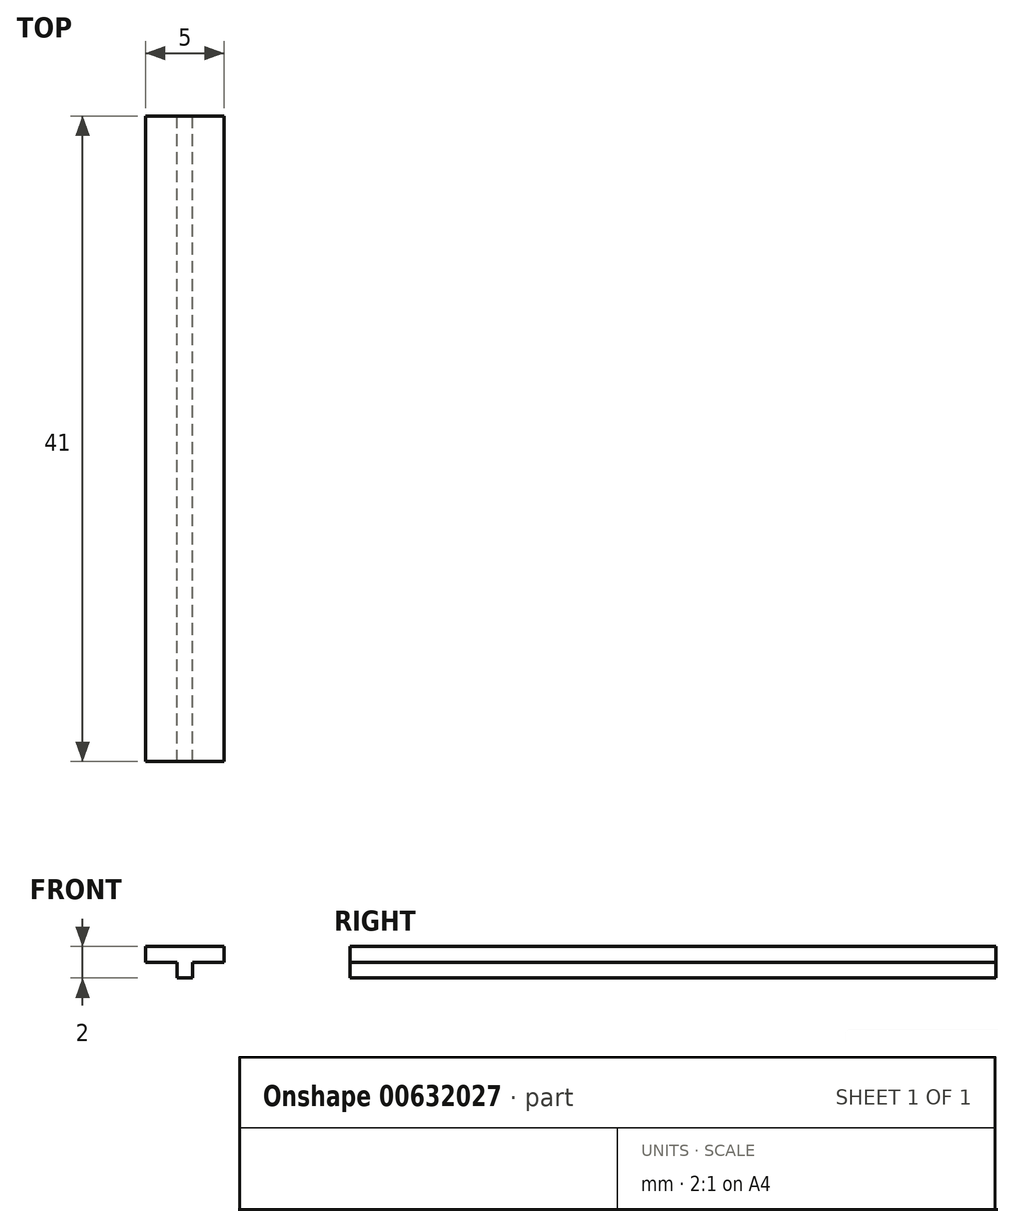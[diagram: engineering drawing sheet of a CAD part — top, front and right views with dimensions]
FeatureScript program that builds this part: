
annotation { "Feature Type Name" : "Feature", "Feature Type Description" : "" }
export const myFeature = defineFeature(function(context is Context, id is Id, definition is map)
    precondition{}
    {
        {
            var Q0;
            Q0=qCreatedBy(makeId("Front.planeOp"),FACE);
            var sketch = newSketch(context, id + "F0", { "sketchPlane" : qUnion([Q0])});
            skLineSegment(sketch, "E0.bottom", {"start": v(2.5, 0.5) * mm, "end": v(-2.5, 0.5) * mm});
            skLineSegment(sketch, "E0.top", {"start": v(2.5, -0.5) * mm, "end": v(-2.5, -0.5) * mm});
            skLineSegment(sketch, "E0.left", {"start": v(2.5, 0.5) * mm, "end": v(2.5, -0.5) * mm});
            skLineSegment(sketch, "E0.right", {"start": v(-2.5, 0.5) * mm, "end": v(-2.5, -0.5) * mm});
            skPoint(sketch, "E0.middle", {"position": v(0, 0) * mm});
            skLineSegment(sketch, "E1", {"start": v(-0.5, -0.5) * mm, "end": v(-0.5, -1.5) * mm});
            skLineSegment(sketch, "E2", {"start": v(-0.5, -1.5) * mm, "end": v(0.5, -1.5) * mm});
            skLineSegment(sketch, "E3", {"start": v(0.5, -1.5) * mm, "end": v(0.5, -0.5) * mm});
            skSolve(sketch);
        }
        {
            var Q0;
            Q0 = qSketchRegion(id + "F0", true);
            extrude(context, id + "F1", {"entities" : qUnion([Q0]), "depth" : 41 * mm, "offsetDistance" : 25 * mm});
        }
    });
